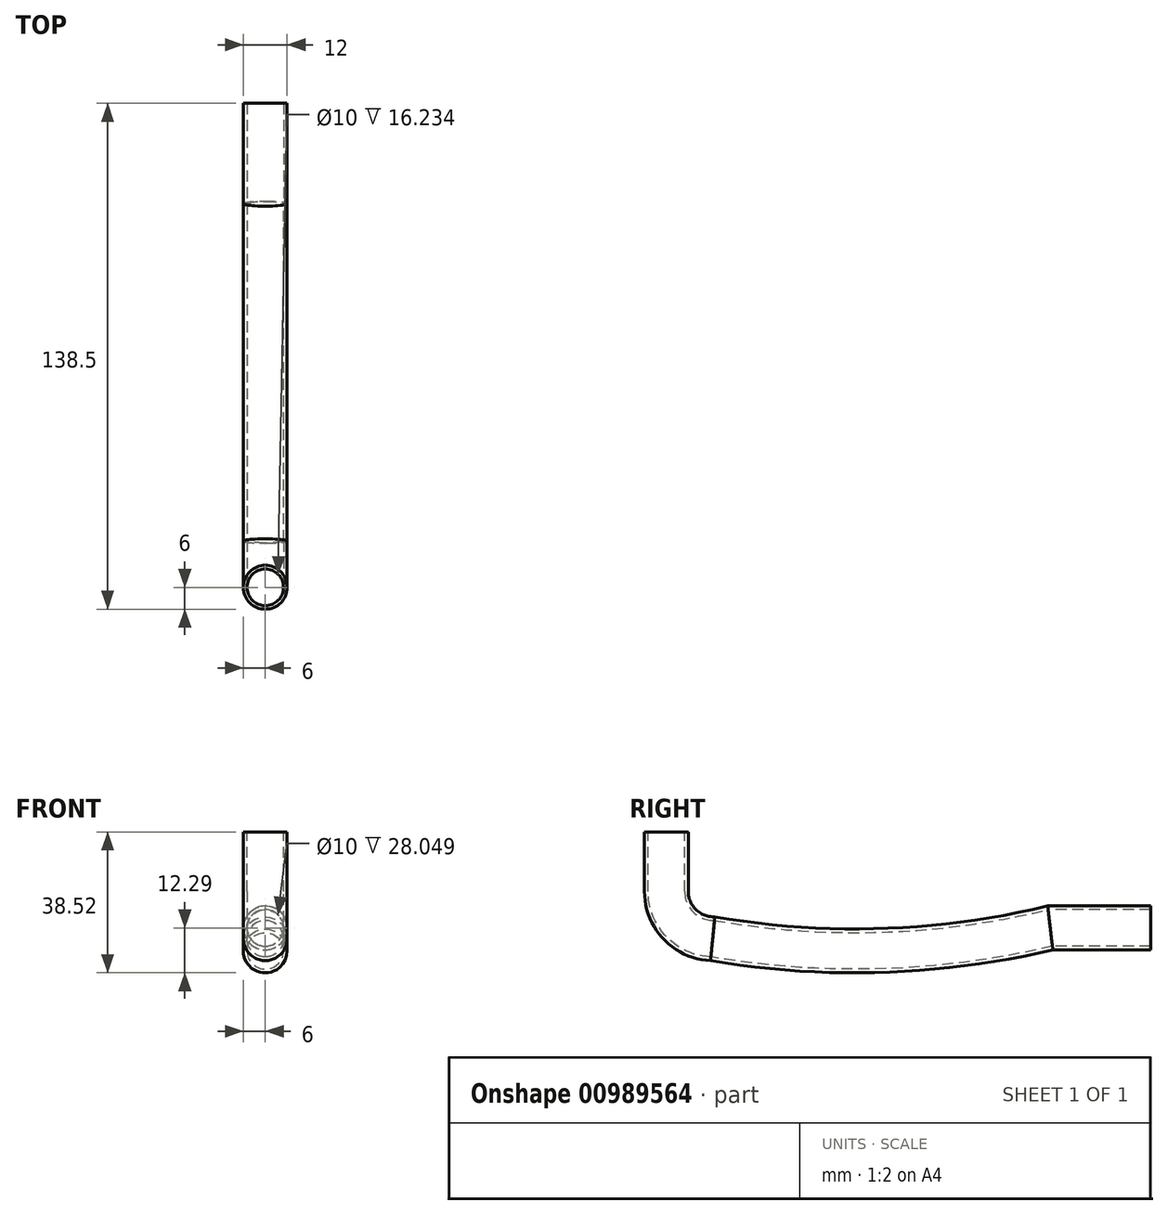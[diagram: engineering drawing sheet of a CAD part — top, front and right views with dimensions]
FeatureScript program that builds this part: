
annotation { "Feature Type Name" : "Feature", "Feature Type Description" : "" }
export const myFeature = defineFeature(function(context is Context, id is Id, definition is map)
    precondition{}
    {
        {
            var Q0;
            Q0=qCreatedBy(makeId("Front.planeOp"), FACE);
            var sketch = newSketch(context, id + "F0", { "sketchPlane" : qUnion([Q0])});
            skCircle(sketch, "E0", {"center": v(0, 0) * mm, "radius": 6 * mm});
            skCircle(sketch, "E1", {"center": v(0, 0) * mm, "radius": 5 * mm});
            skSolve(sketch);
        }
        {
            var Q0;
            Q0=qCreatedBy(makeId("Right.planeOp"), FACE);
            var sketch = newSketch(context, id + "F1", { "sketchPlane" : qUnion([Q0])});
            skLineSegment(sketch, "E2", {"start": v(0, 0) * mm, "end": v(-27.46, 0) * mm});
            skLineSegment(sketch, "E3", {"start": v(-132.5, 10) * mm, "end": v(-132.5, 26.23) * mm});
            skArc(sketch, "E4", {"start": v(-132.5, 10) * mm, "mid": v(-128.8, 0.93) * mm, "end": v(-119.82, -2.96) * mm});
            skArc(sketch, "E5", {"start": v(-119.82, -2.96) * mm, "mid": v(-73.49, -6.17) * mm, "end": v(-27.46, 0) * mm});
            skSolve(sketch);
        }
        {
            var Q0;
            Q0 = qSketchRegion(id + "F0", true);
            var Q1;
            Q1 = qConstructionFilter(qBodyType(qCreatedBy(id + "F1" ,EDGE), BodyType.WIRE), ConstructionObject.NO);
            sweep(context, id + "F2", {"profiles" : qUnion([Q0]), "path" : qUnion([Q1])});
        }
    });
